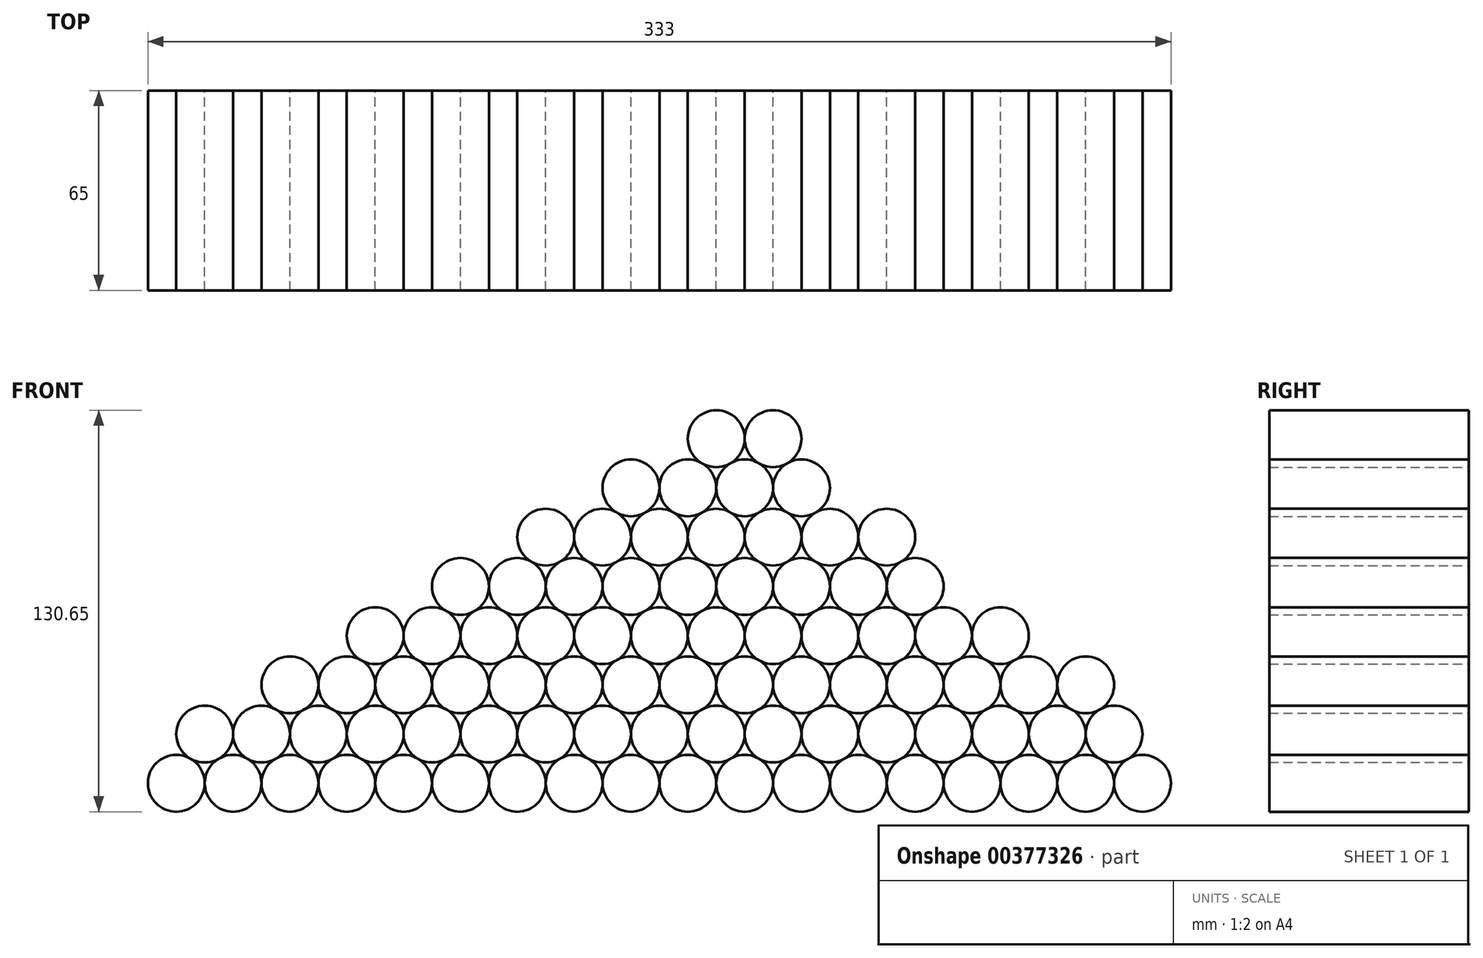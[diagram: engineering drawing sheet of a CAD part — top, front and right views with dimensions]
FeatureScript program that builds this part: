
annotation { "Feature Type Name" : "Feature", "Feature Type Description" : "" }
export const myFeature = defineFeature(function(context is Context, id is Id, definition is map)
    precondition{}
    {
        {
            var Q0;
            Q0=qCreatedBy(makeId("Front.planeOp"),FACE);
            var sketch = newSketch(context, id + "F0", { "sketchPlane" : qUnion([Q0])});
            skLineSegment(sketch, "E0", {"start": v(-257.65, 87.7) * mm, "end": v(102.35, 87.7) * mm, "construction": true});
            skLineSegment(sketch, "E1", {"start": v(16.65, 252.52) * mm, "end": v(-257.65, 87.7) * mm, "construction": true});
            skLineSegment(sketch, "E2", {"start": v(102.35, 87.7) * mm, "end": v(117.67, 100.56) * mm, "construction": true});
            skLineSegment(sketch, "E3", {"start": v(-6.85, 213.41) * mm, "end": v(16.65, 252.52) * mm, "construction": true});
            skLineSegment(sketch, "E4", {"start": v(117.67, 100.56) * mm, "end": v(-6.85, 213.41) * mm, "construction": true});
            skLineSegment(sketch, "E5", {"start": v(-226.86, 106.2) * mm, "end": v(-226.86, 87.7) * mm, "construction": true});
            skCircle(sketch, "E6", {"center": v(98.99, 96.96) * mm, "radius": 9.25 * mm});
            skCircle(sketch, "E7", {"center": v(80.49, 96.96) * mm, "radius": 9.25 * mm});
            skCircle(sketch, "E8", {"center": v(43.49, 96.96) * mm, "radius": 9.25 * mm});
            skCircle(sketch, "E9", {"center": v(24.99, 96.96) * mm, "radius": 9.25 * mm});
            skCircle(sketch, "E10", {"center": v(61.99, 96.96) * mm, "radius": 9.25 * mm});
            skCircle(sketch, "E11", {"center": v(-104.51, 96.96) * mm, "radius": 9.25 * mm});
            skCircle(sketch, "E12", {"center": v(71.24, 112.98) * mm, "radius": 9.25 * mm});
            skCircle(sketch, "E13", {"center": v(-86.01, 96.96) * mm, "radius": 9.25 * mm});
            skCircle(sketch, "E14", {"center": v(-67.51, 96.96) * mm, "radius": 9.25 * mm});
            skCircle(sketch, "E15", {"center": v(-49.01, 96.96) * mm, "radius": 9.25 * mm});
            skCircle(sketch, "E16", {"center": v(-30.51, 96.96) * mm, "radius": 9.25 * mm});
            skCircle(sketch, "E17", {"center": v(-12.01, 96.96) * mm, "radius": 9.25 * mm});
            skCircle(sketch, "E18", {"center": v(89.74, 112.98) * mm, "radius": 9.25 * mm});
            skCircle(sketch, "E19", {"center": v(6.49, 96.96) * mm, "radius": 9.25 * mm});
            skCircle(sketch, "E20", {"center": v(-215.51, 96.96) * mm, "radius": 9.25 * mm});
            skCircle(sketch, "E21", {"center": v(-197.01, 96.96) * mm, "radius": 9.25 * mm});
            skCircle(sketch, "E22", {"center": v(-169.26, 112.98) * mm, "radius": 9.25 * mm});
            skCircle(sketch, "E23", {"center": v(-178.51, 96.96) * mm, "radius": 9.25 * mm});
            skCircle(sketch, "E24", {"center": v(-160.01, 96.96) * mm, "radius": 9.25 * mm});
            skCircle(sketch, "E25", {"center": v(-141.51, 96.96) * mm, "radius": 9.25 * mm});
            skCircle(sketch, "E26", {"center": v(-123.01, 96.96) * mm, "radius": 9.25 * mm});
            skCircle(sketch, "E27", {"center": v(-187.76, 112.98) * mm, "radius": 9.25 * mm});
            skCircle(sketch, "E28", {"center": v(-150.76, 112.98) * mm, "radius": 9.25 * mm});
            skCircle(sketch, "E29", {"center": v(-132.26, 112.98) * mm, "radius": 9.25 * mm});
            skCircle(sketch, "E30", {"center": v(-113.76, 112.98) * mm, "radius": 9.25 * mm});
            skCircle(sketch, "E31", {"center": v(-76.76, 112.98) * mm, "radius": 9.25 * mm});
            skCircle(sketch, "E32", {"center": v(-95.26, 112.98) * mm, "radius": 9.25 * mm});
            skCircle(sketch, "E33", {"center": v(-141.51, 129) * mm, "radius": 9.25 * mm});
            skCircle(sketch, "E34", {"center": v(-123.01, 129) * mm, "radius": 9.25 * mm});
            skCircle(sketch, "E35", {"center": v(-104.51, 129) * mm, "radius": 9.25 * mm});
            skCircle(sketch, "E36", {"center": v(-86.01, 129) * mm, "radius": 9.25 * mm});
            skCircle(sketch, "E37", {"center": v(-160.01, 129) * mm, "radius": 9.25 * mm});
            skCircle(sketch, "E38", {"center": v(6.49, 129) * mm, "radius": 9.25 * mm});
            skCircle(sketch, "E39", {"center": v(-12.01, 129) * mm, "radius": 9.25 * mm});
            skCircle(sketch, "E40", {"center": v(-30.51, 129) * mm, "radius": 9.25 * mm});
            skCircle(sketch, "E41", {"center": v(-67.51, 129) * mm, "radius": 9.25 * mm});
            skCircle(sketch, "E42", {"center": v(-39.76, 112.98) * mm, "radius": 9.25 * mm});
            skCircle(sketch, "E43", {"center": v(-49.01, 129) * mm, "radius": 9.25 * mm});
            skCircle(sketch, "E44", {"center": v(-21.26, 112.98) * mm, "radius": 9.25 * mm});
            skCircle(sketch, "E45", {"center": v(-58.26, 112.98) * mm, "radius": 9.25 * mm});
            skCircle(sketch, "E46", {"center": v(-2.76, 112.98) * mm, "radius": 9.25 * mm});
            skCircle(sketch, "E47", {"center": v(15.74, 112.98) * mm, "radius": 9.25 * mm});
            skCircle(sketch, "E48", {"center": v(34.24, 112.98) * mm, "radius": 9.25 * mm});
            skCircle(sketch, "E49", {"center": v(52.74, 112.98) * mm, "radius": 9.25 * mm});
            skCircle(sketch, "E50", {"center": v(-95.26, 145.02) * mm, "radius": 9.25 * mm});
            skCircle(sketch, "E51", {"center": v(-76.76, 145.02) * mm, "radius": 9.25 * mm});
            skCircle(sketch, "E52", {"center": v(-58.26, 145.02) * mm, "radius": 9.25 * mm});
            skCircle(sketch, "E53", {"center": v(-39.76, 145.02) * mm, "radius": 9.25 * mm});
            skCircle(sketch, "E54", {"center": v(-21.26, 145.02) * mm, "radius": 9.25 * mm});
            skCircle(sketch, "E55", {"center": v(-2.76, 145.02) * mm, "radius": 9.25 * mm});
            skCircle(sketch, "E56", {"center": v(15.74, 145.02) * mm, "radius": 9.25 * mm});
            skCircle(sketch, "E57", {"center": v(61.99, 129) * mm, "radius": 9.25 * mm});
            skCircle(sketch, "E58", {"center": v(43.49, 129) * mm, "radius": 9.25 * mm});
            skCircle(sketch, "E59", {"center": v(24.99, 129) * mm, "radius": 9.25 * mm});
            skCircle(sketch, "E60", {"center": v(-113.76, 145.02) * mm, "radius": 9.25 * mm});
            skCircle(sketch, "E61", {"center": v(-132.26, 145.02) * mm, "radius": 9.25 * mm});
            skCircle(sketch, "E62", {"center": v(-104.51, 161.04) * mm, "radius": 9.25 * mm});
            skCircle(sketch, "E63", {"center": v(-86.01, 161.04) * mm, "radius": 9.25 * mm});
            skCircle(sketch, "E64", {"center": v(-67.51, 161.04) * mm, "radius": 9.25 * mm});
            skCircle(sketch, "E65", {"center": v(-49.01, 161.04) * mm, "radius": 9.25 * mm});
            skCircle(sketch, "E66", {"center": v(-30.51, 161.04) * mm, "radius": 9.25 * mm});
            skCircle(sketch, "E67", {"center": v(-12.01, 161.04) * mm, "radius": 9.25 * mm});
            skCircle(sketch, "E68", {"center": v(6.49, 161.04) * mm, "radius": 9.25 * mm});
            skCircle(sketch, "E69", {"center": v(34.24, 145.02) * mm, "radius": 9.25 * mm});
            skCircle(sketch, "E70", {"center": v(-76.76, 177.07) * mm, "radius": 9.25 * mm});
            skCircle(sketch, "E71", {"center": v(-2.76, 177.07) * mm, "radius": 9.25 * mm});
            skCircle(sketch, "E72", {"center": v(-21.26, 177.07) * mm, "radius": 9.25 * mm});
            skCircle(sketch, "E73", {"center": v(-39.76, 177.07) * mm, "radius": 9.25 * mm});
            skCircle(sketch, "E74", {"center": v(-30.51, 193.09) * mm, "radius": 9.25 * mm});
            skCircle(sketch, "E75", {"center": v(-58.26, 177.07) * mm, "radius": 9.25 * mm});
            skCircle(sketch, "E76", {"center": v(24.99, 161.04) * mm, "radius": 9.25 * mm});
            skCircle(sketch, "E77", {"center": v(52.74, 145.02) * mm, "radius": 9.25 * mm});
            skCircle(sketch, "E78", {"center": v(-49.01, 193.09) * mm, "radius": 9.25 * mm});
            skCircle(sketch, "E79", {"center": v(-12.01, 193.09) * mm, "radius": 9.25 * mm});
            skCircle(sketch, "E80", {"center": v(-21.26, 209.1) * mm, "radius": 9.25 * mm});
            skCircle(sketch, "E81", {"center": v(15.74, 177.07) * mm, "radius": 9.25 * mm});
            skCircle(sketch, "E82", {"center": v(-206.26, 112.98) * mm, "radius": 9.25 * mm});
            skCircle(sketch, "E83", {"center": v(-178.51, 129) * mm, "radius": 9.25 * mm});
            skCircle(sketch, "E84", {"center": v(-150.76, 145.02) * mm, "radius": 9.25 * mm});
            skCircle(sketch, "E85", {"center": v(-123.01, 161.04) * mm, "radius": 9.25 * mm});
            skCircle(sketch, "E86", {"center": v(-95.26, 177.07) * mm, "radius": 9.25 * mm});
            skCircle(sketch, "E87", {"center": v(-67.51, 193.09) * mm, "radius": 9.25 * mm});
            skCircle(sketch, "E88", {"center": v(-39.76, 209.1) * mm, "radius": 9.25 * mm});
            skCircle(sketch, "E89", {"center": v(80.49, 129) * mm, "radius": 9.25 * mm});
            skSolve(sketch);
        }
        {
            var Q0;
            {var subQ0=sQuery(id+"F0.wireOp",EDGE,"E6");var subQ1=makeQuery(id+"F0.imprint","INTERSECT",VERTEX,{"derivedFrom":[subQ0,sQuery(id+"F0.wireOp",EDGE,"E7")]});Q0=makeQuery(id+"F0.imprint","IMPRINT",FACE,{"disambiguationData":[TD([[makeQuery(id+"F0.imprint","IMPRINT",EDGE,{"disambiguationData":[TD([[subQ1,1.0]])],"derivedFrom":subQ0}),1.0]])]});}
            var Q1;
            {var subQ0=sQuery(id+"F0.wireOp",EDGE,"E77");var subQ1=makeQuery(id+"F0.imprint","INTERSECT",VERTEX,{"derivedFrom":[sQuery(id+"F0.wireOp",EDGE,"E69"),subQ0]});Q1=makeQuery(id+"F0.imprint","IMPRINT",FACE,{"disambiguationData":[TD([[makeQuery(id+"F0.imprint","IMPRINT",EDGE,{"disambiguationData":[TD([[subQ1,-1.0]])],"derivedFrom":subQ0}),1.0]])]});}
            var Q2;
            {var subQ0=sQuery(id+"F0.wireOp",EDGE,"E80");var subQ1=makeQuery(id+"F0.imprint","INTERSECT",VERTEX,{"derivedFrom":[subQ0,sQuery(id+"F0.wireOp",EDGE,"E88")]});Q2=makeQuery(id+"F0.imprint","IMPRINT",FACE,{"disambiguationData":[TD([[makeQuery(id+"F0.imprint","IMPRINT",EDGE,{"disambiguationData":[TD([[subQ1,-1.0]])],"derivedFrom":subQ0}),1.0]])]});}
            var Q3;
            {var subQ0=sQuery(id+"F0.wireOp",EDGE,"E81");var subQ1=makeQuery(id+"F0.imprint","INTERSECT",VERTEX,{"derivedFrom":[sQuery(id+"F0.wireOp",EDGE,"E71"),subQ0]});Q3=makeQuery(id+"F0.imprint","IMPRINT",FACE,{"disambiguationData":[TD([[makeQuery(id+"F0.imprint","IMPRINT",EDGE,{"disambiguationData":[TD([[subQ1,-1.0]])],"derivedFrom":subQ0}),1.0]])]});}
            var Q4;
            {var subQ0=sQuery(id+"F0.wireOp",EDGE,"E82");var subQ1=makeQuery(id+"F0.imprint","INTERSECT",VERTEX,{"derivedFrom":[sQuery(id+"F0.wireOp",EDGE,"E20"),subQ0]});Q4=makeQuery(id+"F0.imprint","IMPRINT",FACE,{"disambiguationData":[TD([[makeQuery(id+"F0.imprint","IMPRINT",EDGE,{"disambiguationData":[TD([[subQ1,1.0]])],"derivedFrom":subQ0}),1.0]])]});}
            var Q5;
            {var subQ0=sQuery(id+"F0.wireOp",EDGE,"E83");var subQ1=makeQuery(id+"F0.imprint","INTERSECT",VERTEX,{"derivedFrom":[sQuery(id+"F0.wireOp",EDGE,"E27"),subQ0]});Q5=makeQuery(id+"F0.imprint","IMPRINT",FACE,{"disambiguationData":[TD([[makeQuery(id+"F0.imprint","IMPRINT",EDGE,{"disambiguationData":[TD([[subQ1,1.0]])],"derivedFrom":subQ0}),1.0]])]});}
            var Q6;
            {var subQ0=sQuery(id+"F0.wireOp",EDGE,"E84");var subQ1=makeQuery(id+"F0.imprint","INTERSECT",VERTEX,{"derivedFrom":[sQuery(id+"F0.wireOp",EDGE,"E37"),subQ0]});Q6=makeQuery(id+"F0.imprint","IMPRINT",FACE,{"disambiguationData":[TD([[makeQuery(id+"F0.imprint","IMPRINT",EDGE,{"disambiguationData":[TD([[subQ1,1.0]])],"derivedFrom":subQ0}),1.0]])]});}
            var Q7;
            {var subQ0=sQuery(id+"F0.wireOp",EDGE,"E85");var subQ1=makeQuery(id+"F0.imprint","INTERSECT",VERTEX,{"derivedFrom":[sQuery(id+"F0.wireOp",EDGE,"E61"),subQ0]});Q7=makeQuery(id+"F0.imprint","IMPRINT",FACE,{"disambiguationData":[TD([[makeQuery(id+"F0.imprint","IMPRINT",EDGE,{"disambiguationData":[TD([[subQ1,1.0]])],"derivedFrom":subQ0}),1.0]])]});}
            var Q8;
            {var subQ0=sQuery(id+"F0.wireOp",EDGE,"E86");var subQ1=makeQuery(id+"F0.imprint","INTERSECT",VERTEX,{"derivedFrom":[sQuery(id+"F0.wireOp",EDGE,"E62"),subQ0]});Q8=makeQuery(id+"F0.imprint","IMPRINT",FACE,{"disambiguationData":[TD([[makeQuery(id+"F0.imprint","IMPRINT",EDGE,{"disambiguationData":[TD([[subQ1,1.0]])],"derivedFrom":subQ0}),1.0]])]});}
            var Q9;
            {var subQ0=sQuery(id+"F0.wireOp",EDGE,"E87");var subQ1=makeQuery(id+"F0.imprint","INTERSECT",VERTEX,{"derivedFrom":[sQuery(id+"F0.wireOp",EDGE,"E70"),subQ0]});Q9=makeQuery(id+"F0.imprint","IMPRINT",FACE,{"disambiguationData":[TD([[makeQuery(id+"F0.imprint","IMPRINT",EDGE,{"disambiguationData":[TD([[subQ1,1.0]])],"derivedFrom":subQ0}),1.0]])]});}
            var Q10;
            {var subQ0=sQuery(id+"F0.wireOp",EDGE,"E88");var subQ1=makeQuery(id+"F0.imprint","INTERSECT",VERTEX,{"derivedFrom":[sQuery(id+"F0.wireOp",EDGE,"E78"),subQ0]});Q10=makeQuery(id+"F0.imprint","IMPRINT",FACE,{"disambiguationData":[TD([[makeQuery(id+"F0.imprint","IMPRINT",EDGE,{"disambiguationData":[TD([[subQ1,1.0]])],"derivedFrom":subQ0}),1.0]])]});}
            var Q11;
            {var subQ0=sQuery(id+"F0.wireOp",EDGE,"E89");var subQ1=makeQuery(id+"F0.imprint","INTERSECT",VERTEX,{"derivedFrom":[sQuery(id+"F0.wireOp",EDGE,"E57"),subQ0]});Q11=makeQuery(id+"F0.imprint","IMPRINT",FACE,{"disambiguationData":[TD([[makeQuery(id+"F0.imprint","IMPRINT",EDGE,{"disambiguationData":[TD([[subQ1,-1.0]])],"derivedFrom":subQ0}),1.0]])]});}
            var Q12;
            {var subQ0=sQuery(id+"F0.wireOp",EDGE,"E7");var subQ1=makeQuery(id+"F0.imprint","INTERSECT",VERTEX,{"derivedFrom":[sQuery(id+"F0.wireOp",EDGE,"E6"),subQ0]});Q12=makeQuery(id+"F0.imprint","IMPRINT",FACE,{"disambiguationData":[TD([[makeQuery(id+"F0.imprint","IMPRINT",EDGE,{"disambiguationData":[TD([[subQ1,-1.0]])],"derivedFrom":subQ0}),1.0]])]});}
            var Q13;
            {var subQ0=sQuery(id+"F0.wireOp",EDGE,"E8");var subQ1=makeQuery(id+"F0.imprint","INTERSECT",VERTEX,{"derivedFrom":[subQ0,sQuery(id+"F0.wireOp",EDGE,"E10")]});Q13=makeQuery(id+"F0.imprint","IMPRINT",FACE,{"disambiguationData":[TD([[makeQuery(id+"F0.imprint","IMPRINT",EDGE,{"disambiguationData":[TD([[subQ1,-1.0]])],"derivedFrom":subQ0}),1.0]])]});}
            var Q14;
            {var subQ0=sQuery(id+"F0.wireOp",EDGE,"E9");var subQ1=makeQuery(id+"F0.imprint","INTERSECT",VERTEX,{"derivedFrom":[sQuery(id+"F0.wireOp",EDGE,"E8"),subQ0]});Q14=makeQuery(id+"F0.imprint","IMPRINT",FACE,{"disambiguationData":[TD([[makeQuery(id+"F0.imprint","IMPRINT",EDGE,{"disambiguationData":[TD([[subQ1,-1.0]])],"derivedFrom":subQ0}),1.0]])]});}
            var Q15;
            {var subQ0=sQuery(id+"F0.wireOp",EDGE,"E10");var subQ1=makeQuery(id+"F0.imprint","INTERSECT",VERTEX,{"derivedFrom":[sQuery(id+"F0.wireOp",EDGE,"E7"),subQ0]});Q15=makeQuery(id+"F0.imprint","IMPRINT",FACE,{"disambiguationData":[TD([[makeQuery(id+"F0.imprint","IMPRINT",EDGE,{"disambiguationData":[TD([[subQ1,-1.0]])],"derivedFrom":subQ0}),1.0]])]});}
            var Q16;
            {var subQ0=sQuery(id+"F0.wireOp",EDGE,"E11");var subQ1=makeQuery(id+"F0.imprint","INTERSECT",VERTEX,{"derivedFrom":[subQ0,sQuery(id+"F0.wireOp",EDGE,"E13")]});Q16=makeQuery(id+"F0.imprint","IMPRINT",FACE,{"disambiguationData":[TD([[makeQuery(id+"F0.imprint","IMPRINT",EDGE,{"disambiguationData":[TD([[subQ1,-1.0]])],"derivedFrom":subQ0}),1.0]])]});}
            var Q17;
            {var subQ0=sQuery(id+"F0.wireOp",EDGE,"E13");var subQ1=makeQuery(id+"F0.imprint","INTERSECT",VERTEX,{"derivedFrom":[subQ0,sQuery(id+"F0.wireOp",EDGE,"E14")]});Q17=makeQuery(id+"F0.imprint","IMPRINT",FACE,{"disambiguationData":[TD([[makeQuery(id+"F0.imprint","IMPRINT",EDGE,{"disambiguationData":[TD([[subQ1,-1.0]])],"derivedFrom":subQ0}),1.0]])]});}
            var Q18;
            {var subQ0=sQuery(id+"F0.wireOp",EDGE,"E14");var subQ1=makeQuery(id+"F0.imprint","INTERSECT",VERTEX,{"derivedFrom":[subQ0,sQuery(id+"F0.wireOp",EDGE,"E15")]});Q18=makeQuery(id+"F0.imprint","IMPRINT",FACE,{"disambiguationData":[TD([[makeQuery(id+"F0.imprint","IMPRINT",EDGE,{"disambiguationData":[TD([[subQ1,-1.0]])],"derivedFrom":subQ0}),1.0]])]});}
            var Q19;
            {var subQ0=sQuery(id+"F0.wireOp",EDGE,"E15");var subQ1=makeQuery(id+"F0.imprint","INTERSECT",VERTEX,{"derivedFrom":[subQ0,sQuery(id+"F0.wireOp",EDGE,"E16")]});Q19=makeQuery(id+"F0.imprint","IMPRINT",FACE,{"disambiguationData":[TD([[makeQuery(id+"F0.imprint","IMPRINT",EDGE,{"disambiguationData":[TD([[subQ1,-1.0]])],"derivedFrom":subQ0}),1.0]])]});}
            var Q20;
            {var subQ0=sQuery(id+"F0.wireOp",EDGE,"E16");var subQ1=makeQuery(id+"F0.imprint","INTERSECT",VERTEX,{"derivedFrom":[subQ0,sQuery(id+"F0.wireOp",EDGE,"E17")]});Q20=makeQuery(id+"F0.imprint","IMPRINT",FACE,{"disambiguationData":[TD([[makeQuery(id+"F0.imprint","IMPRINT",EDGE,{"disambiguationData":[TD([[subQ1,-1.0]])],"derivedFrom":subQ0}),1.0]])]});}
            var Q21;
            {var subQ0=sQuery(id+"F0.wireOp",EDGE,"E17");var subQ1=makeQuery(id+"F0.imprint","INTERSECT",VERTEX,{"derivedFrom":[subQ0,sQuery(id+"F0.wireOp",EDGE,"E19")]});Q21=makeQuery(id+"F0.imprint","IMPRINT",FACE,{"disambiguationData":[TD([[makeQuery(id+"F0.imprint","IMPRINT",EDGE,{"disambiguationData":[TD([[subQ1,-1.0]])],"derivedFrom":subQ0}),1.0]])]});}
            var Q22;
            {var subQ0=sQuery(id+"F0.wireOp",EDGE,"E18");var subQ1=makeQuery(id+"F0.imprint","INTERSECT",VERTEX,{"derivedFrom":[subQ0,sQuery(id+"F0.wireOp",EDGE,"E89")]});Q22=makeQuery(id+"F0.imprint","IMPRINT",FACE,{"disambiguationData":[TD([[makeQuery(id+"F0.imprint","IMPRINT",EDGE,{"disambiguationData":[TD([[subQ1,-1.0]])],"derivedFrom":subQ0}),1.0]])]});}
            var Q23;
            {var subQ0=sQuery(id+"F0.wireOp",EDGE,"E19");var subQ1=makeQuery(id+"F0.imprint","INTERSECT",VERTEX,{"derivedFrom":[sQuery(id+"F0.wireOp",EDGE,"E9"),subQ0]});Q23=makeQuery(id+"F0.imprint","IMPRINT",FACE,{"disambiguationData":[TD([[makeQuery(id+"F0.imprint","IMPRINT",EDGE,{"disambiguationData":[TD([[subQ1,-1.0]])],"derivedFrom":subQ0}),1.0]])]});}
            var Q24;
            {var subQ0=sQuery(id+"F0.wireOp",EDGE,"E21");var subQ1=makeQuery(id+"F0.imprint","INTERSECT",VERTEX,{"derivedFrom":[subQ0,sQuery(id+"F0.wireOp",EDGE,"E23")]});Q24=makeQuery(id+"F0.imprint","IMPRINT",FACE,{"disambiguationData":[TD([[makeQuery(id+"F0.imprint","IMPRINT",EDGE,{"disambiguationData":[TD([[subQ1,-1.0]])],"derivedFrom":subQ0}),1.0]])]});}
            var Q25;
            {var subQ0=sQuery(id+"F0.wireOp",EDGE,"E23");var subQ1=makeQuery(id+"F0.imprint","INTERSECT",VERTEX,{"derivedFrom":[subQ0,sQuery(id+"F0.wireOp",EDGE,"E24")]});Q25=makeQuery(id+"F0.imprint","IMPRINT",FACE,{"disambiguationData":[TD([[makeQuery(id+"F0.imprint","IMPRINT",EDGE,{"disambiguationData":[TD([[subQ1,-1.0]])],"derivedFrom":subQ0}),1.0]])]});}
            var Q26;
            {var subQ0=sQuery(id+"F0.wireOp",EDGE,"E24");var subQ1=makeQuery(id+"F0.imprint","INTERSECT",VERTEX,{"derivedFrom":[subQ0,sQuery(id+"F0.wireOp",EDGE,"E25")]});Q26=makeQuery(id+"F0.imprint","IMPRINT",FACE,{"disambiguationData":[TD([[makeQuery(id+"F0.imprint","IMPRINT",EDGE,{"disambiguationData":[TD([[subQ1,-1.0]])],"derivedFrom":subQ0}),1.0]])]});}
            var Q27;
            {var subQ0=sQuery(id+"F0.wireOp",EDGE,"E25");var subQ1=makeQuery(id+"F0.imprint","INTERSECT",VERTEX,{"derivedFrom":[subQ0,sQuery(id+"F0.wireOp",EDGE,"E26")]});Q27=makeQuery(id+"F0.imprint","IMPRINT",FACE,{"disambiguationData":[TD([[makeQuery(id+"F0.imprint","IMPRINT",EDGE,{"disambiguationData":[TD([[subQ1,-1.0]])],"derivedFrom":subQ0}),1.0]])]});}
            var Q28;
            {var subQ0=sQuery(id+"F0.wireOp",EDGE,"E26");var subQ1=makeQuery(id+"F0.imprint","INTERSECT",VERTEX,{"derivedFrom":[sQuery(id+"F0.wireOp",EDGE,"E11"),subQ0]});Q28=makeQuery(id+"F0.imprint","IMPRINT",FACE,{"disambiguationData":[TD([[makeQuery(id+"F0.imprint","IMPRINT",EDGE,{"disambiguationData":[TD([[subQ1,-1.0]])],"derivedFrom":subQ0}),1.0]])]});}
            var Q29;
            {var subQ0=sQuery(id+"F0.wireOp",EDGE,"E76");var subQ1=makeQuery(id+"F0.imprint","INTERSECT",VERTEX,{"derivedFrom":[subQ0,sQuery(id+"F0.wireOp",EDGE,"E81")]});Q29=makeQuery(id+"F0.imprint","IMPRINT",FACE,{"disambiguationData":[TD([[makeQuery(id+"F0.imprint","IMPRINT",EDGE,{"disambiguationData":[TD([[subQ1,-1.0]])],"derivedFrom":subQ0}),1.0]])]});}
            var Q30;
            {var subQ0=sQuery(id+"F0.wireOp",EDGE,"E79");var subQ1=makeQuery(id+"F0.imprint","INTERSECT",VERTEX,{"derivedFrom":[subQ0,sQuery(id+"F0.wireOp",EDGE,"E80")]});Q30=makeQuery(id+"F0.imprint","IMPRINT",FACE,{"disambiguationData":[TD([[makeQuery(id+"F0.imprint","IMPRINT",EDGE,{"disambiguationData":[TD([[subQ1,-1.0]])],"derivedFrom":subQ0}),1.0]])]});}
            var Q31;
            {var subQ0=sQuery(id+"F0.wireOp",EDGE,"E27");var subQ4=makeQuery(id+"F0.imprint","INTERSECT",VERTEX,{"derivedFrom":[subQ0,sQuery(id+"F0.wireOp",EDGE,"E83")]});Q31=makeQuery(id+"F0.imprint","IMPRINT",FACE,{"disambiguationData":[TD([[makeQuery(id+"F0.imprint","IMPRINT",EDGE,{"disambiguationData":[TD([[subQ4,1.0]])],"derivedFrom":subQ0}),1.0]])]});}
            var Q32;
            {var subQ0=sQuery(id+"F0.wireOp",EDGE,"E37");var subQ4=makeQuery(id+"F0.imprint","INTERSECT",VERTEX,{"derivedFrom":[subQ0,sQuery(id+"F0.wireOp",EDGE,"E84")]});Q32=makeQuery(id+"F0.imprint","IMPRINT",FACE,{"disambiguationData":[TD([[makeQuery(id+"F0.imprint","IMPRINT",EDGE,{"disambiguationData":[TD([[subQ4,1.0]])],"derivedFrom":subQ0}),1.0]])]});}
            var Q33;
            {var subQ0=sQuery(id+"F0.wireOp",EDGE,"E57");var subQ4=makeQuery(id+"F0.imprint","INTERSECT",VERTEX,{"derivedFrom":[subQ0,sQuery(id+"F0.wireOp",EDGE,"E77")]});Q33=makeQuery(id+"F0.imprint","IMPRINT",FACE,{"disambiguationData":[TD([[makeQuery(id+"F0.imprint","IMPRINT",EDGE,{"disambiguationData":[TD([[subQ4,1.0]])],"derivedFrom":subQ0}),1.0]])]});}
            var Q34;
            {var subQ0=sQuery(id+"F0.wireOp",EDGE,"E61");var subQ4=makeQuery(id+"F0.imprint","INTERSECT",VERTEX,{"derivedFrom":[subQ0,sQuery(id+"F0.wireOp",EDGE,"E85")]});Q34=makeQuery(id+"F0.imprint","IMPRINT",FACE,{"disambiguationData":[TD([[makeQuery(id+"F0.imprint","IMPRINT",EDGE,{"disambiguationData":[TD([[subQ4,1.0]])],"derivedFrom":subQ0}),1.0]])]});}
            var Q35;
            {var subQ0=sQuery(id+"F0.wireOp",EDGE,"E62");var subQ4=makeQuery(id+"F0.imprint","INTERSECT",VERTEX,{"derivedFrom":[subQ0,sQuery(id+"F0.wireOp",EDGE,"E86")]});Q35=makeQuery(id+"F0.imprint","IMPRINT",FACE,{"disambiguationData":[TD([[makeQuery(id+"F0.imprint","IMPRINT",EDGE,{"disambiguationData":[TD([[subQ4,1.0]])],"derivedFrom":subQ0}),1.0]])]});}
            var Q36;
            {var subQ0=sQuery(id+"F0.wireOp",EDGE,"E69");var subQ4=makeQuery(id+"F0.imprint","INTERSECT",VERTEX,{"derivedFrom":[subQ0,sQuery(id+"F0.wireOp",EDGE,"E76")]});Q36=makeQuery(id+"F0.imprint","IMPRINT",FACE,{"disambiguationData":[TD([[makeQuery(id+"F0.imprint","IMPRINT",EDGE,{"disambiguationData":[TD([[subQ4,1.0]])],"derivedFrom":subQ0}),1.0]])]});}
            var Q37;
            {var subQ0=sQuery(id+"F0.wireOp",EDGE,"E70");var subQ4=makeQuery(id+"F0.imprint","INTERSECT",VERTEX,{"derivedFrom":[subQ0,sQuery(id+"F0.wireOp",EDGE,"E87")]});Q37=makeQuery(id+"F0.imprint","IMPRINT",FACE,{"disambiguationData":[TD([[makeQuery(id+"F0.imprint","IMPRINT",EDGE,{"disambiguationData":[TD([[subQ4,1.0]])],"derivedFrom":subQ0}),1.0]])]});}
            var Q38;
            {var subQ0=sQuery(id+"F0.wireOp",EDGE,"E71");var subQ4=makeQuery(id+"F0.imprint","INTERSECT",VERTEX,{"derivedFrom":[subQ0,sQuery(id+"F0.wireOp",EDGE,"E79")]});Q38=makeQuery(id+"F0.imprint","IMPRINT",FACE,{"disambiguationData":[TD([[makeQuery(id+"F0.imprint","IMPRINT",EDGE,{"disambiguationData":[TD([[subQ4,1.0]])],"derivedFrom":subQ0}),1.0]])]});}
            var Q39;
            {var subQ0=sQuery(id+"F0.wireOp",EDGE,"E78");var subQ4=makeQuery(id+"F0.imprint","INTERSECT",VERTEX,{"derivedFrom":[subQ0,sQuery(id+"F0.wireOp",EDGE,"E88")]});Q39=makeQuery(id+"F0.imprint","IMPRINT",FACE,{"disambiguationData":[TD([[makeQuery(id+"F0.imprint","IMPRINT",EDGE,{"disambiguationData":[TD([[subQ4,1.0]])],"derivedFrom":subQ0}),1.0]])]});}
            var Q40;
            {var subQ0=sQuery(id+"F0.wireOp",EDGE,"E51");var subQ4=makeQuery(id+"F0.imprint","INTERSECT",VERTEX,{"derivedFrom":[subQ0,sQuery(id+"F0.wireOp",EDGE,"E64")]});Q40=makeQuery(id+"F0.imprint","IMPRINT",FACE,{"disambiguationData":[TD([[makeQuery(id+"F0.imprint","IMPRINT",EDGE,{"disambiguationData":[TD([[subQ4,1.0]])],"derivedFrom":subQ0}),1.0]])]});}
            var Q41;
            {var subQ0=sQuery(id+"F0.wireOp",EDGE,"E59");var subQ5=makeQuery(id+"F0.imprint","INTERSECT",VERTEX,{"derivedFrom":[sQuery(id+"F0.wireOp",EDGE,"E58"),subQ0]});Q41=makeQuery(id+"F0.imprint","IMPRINT",FACE,{"disambiguationData":[TD([[makeQuery(id+"F0.imprint","IMPRINT",EDGE,{"disambiguationData":[TD([[subQ5,-1.0]])],"derivedFrom":subQ0}),1.0]])]});}
            var Q42;
            {var subQ0=sQuery(id+"F0.wireOp",EDGE,"E48");var subQ4=makeQuery(id+"F0.imprint","INTERSECT",VERTEX,{"derivedFrom":[subQ0,sQuery(id+"F0.wireOp",EDGE,"E58")]});Q42=makeQuery(id+"F0.imprint","IMPRINT",FACE,{"disambiguationData":[TD([[makeQuery(id+"F0.imprint","IMPRINT",EDGE,{"disambiguationData":[TD([[subQ4,1.0]])],"derivedFrom":subQ0}),1.0]])]});}
            var Q43;
            {var subQ0=sQuery(id+"F0.wireOp",EDGE,"E46");var subQ4=makeQuery(id+"F0.imprint","INTERSECT",VERTEX,{"derivedFrom":[sQuery(id+"F0.wireOp",EDGE,"E38"),subQ0]});Q43=makeQuery(id+"F0.imprint","IMPRINT",FACE,{"disambiguationData":[TD([[makeQuery(id+"F0.imprint","IMPRINT",EDGE,{"disambiguationData":[TD([[subQ4,1.0]])],"derivedFrom":subQ0}),1.0]])]});}
            var Q44;
            {var subQ0=sQuery(id+"F0.wireOp",EDGE,"E39");var subQ5=makeQuery(id+"F0.imprint","INTERSECT",VERTEX,{"derivedFrom":[sQuery(id+"F0.wireOp",EDGE,"E38"),subQ0]});Q44=makeQuery(id+"F0.imprint","IMPRINT",FACE,{"disambiguationData":[TD([[makeQuery(id+"F0.imprint","IMPRINT",EDGE,{"disambiguationData":[TD([[subQ5,-1.0]])],"derivedFrom":subQ0}),1.0]])]});}
            var Q45;
            {var subQ0=sQuery(id+"F0.wireOp",EDGE,"E49");var subQ5=makeQuery(id+"F0.imprint","INTERSECT",VERTEX,{"derivedFrom":[sQuery(id+"F0.wireOp",EDGE,"E12"),subQ0]});Q45=makeQuery(id+"F0.imprint","IMPRINT",FACE,{"disambiguationData":[TD([[makeQuery(id+"F0.imprint","IMPRINT",EDGE,{"disambiguationData":[TD([[subQ5,-1.0]])],"derivedFrom":subQ0}),1.0]])]});}
            var Q46;
            {var subQ0=sQuery(id+"F0.wireOp",EDGE,"E55");var subQ4=makeQuery(id+"F0.imprint","INTERSECT",VERTEX,{"derivedFrom":[subQ0,sQuery(id+"F0.wireOp",EDGE,"E68")]});Q46=makeQuery(id+"F0.imprint","IMPRINT",FACE,{"disambiguationData":[TD([[makeQuery(id+"F0.imprint","IMPRINT",EDGE,{"disambiguationData":[TD([[subQ4,1.0]])],"derivedFrom":subQ0}),1.0]])]});}
            var Q47;
            {var subQ0=sQuery(id+"F0.wireOp",EDGE,"E73");var subQ5=makeQuery(id+"F0.imprint","INTERSECT",VERTEX,{"derivedFrom":[sQuery(id+"F0.wireOp",EDGE,"E72"),subQ0]});Q47=makeQuery(id+"F0.imprint","IMPRINT",FACE,{"disambiguationData":[TD([[makeQuery(id+"F0.imprint","IMPRINT",EDGE,{"disambiguationData":[TD([[subQ5,-1.0]])],"derivedFrom":subQ0}),1.0]])]});}
            var Q48;
            {var subQ0=sQuery(id+"F0.wireOp",EDGE,"E34");var subQ4=makeQuery(id+"F0.imprint","INTERSECT",VERTEX,{"derivedFrom":[subQ0,sQuery(id+"F0.wireOp",EDGE,"E60")]});Q48=makeQuery(id+"F0.imprint","IMPRINT",FACE,{"disambiguationData":[TD([[makeQuery(id+"F0.imprint","IMPRINT",EDGE,{"disambiguationData":[TD([[subQ4,1.0]])],"derivedFrom":subQ0}),1.0]])]});}
            var Q49;
            {var subQ0=sQuery(id+"F0.wireOp",EDGE,"E67");var subQ4=makeQuery(id+"F0.imprint","INTERSECT",VERTEX,{"derivedFrom":[subQ0,sQuery(id+"F0.wireOp",EDGE,"E71")]});Q49=makeQuery(id+"F0.imprint","IMPRINT",FACE,{"disambiguationData":[TD([[makeQuery(id+"F0.imprint","IMPRINT",EDGE,{"disambiguationData":[TD([[subQ4,1.0]])],"derivedFrom":subQ0}),1.0]])]});}
            var Q50;
            {var subQ0=sQuery(id+"F0.wireOp",EDGE,"E31");var subQ4=makeQuery(id+"F0.imprint","INTERSECT",VERTEX,{"derivedFrom":[subQ0,sQuery(id+"F0.wireOp",EDGE,"E41")]});Q50=makeQuery(id+"F0.imprint","IMPRINT",FACE,{"disambiguationData":[TD([[makeQuery(id+"F0.imprint","IMPRINT",EDGE,{"disambiguationData":[TD([[subQ4,1.0]])],"derivedFrom":subQ0}),1.0]])]});}
            var Q51;
            {var subQ0=sQuery(id+"F0.wireOp",EDGE,"E41");var subQ4=makeQuery(id+"F0.imprint","INTERSECT",VERTEX,{"derivedFrom":[subQ0,sQuery(id+"F0.wireOp",EDGE,"E52")]});Q51=makeQuery(id+"F0.imprint","IMPRINT",FACE,{"disambiguationData":[TD([[makeQuery(id+"F0.imprint","IMPRINT",EDGE,{"disambiguationData":[TD([[subQ4,1.0]])],"derivedFrom":subQ0}),1.0]])]});}
            var Q52;
            {var subQ0=sQuery(id+"F0.wireOp",EDGE,"E74");var subQ4=makeQuery(id+"F0.imprint","INTERSECT",VERTEX,{"derivedFrom":[subQ0,sQuery(id+"F0.wireOp",EDGE,"E80")]});Q52=makeQuery(id+"F0.imprint","IMPRINT",FACE,{"disambiguationData":[TD([[makeQuery(id+"F0.imprint","IMPRINT",EDGE,{"disambiguationData":[TD([[subQ4,1.0]])],"derivedFrom":subQ0}),1.0]])]});}
            var Q53;
            {var subQ0=sQuery(id+"F0.wireOp",EDGE,"E63");var subQ4=makeQuery(id+"F0.imprint","INTERSECT",VERTEX,{"derivedFrom":[subQ0,sQuery(id+"F0.wireOp",EDGE,"E70")]});Q53=makeQuery(id+"F0.imprint","IMPRINT",FACE,{"disambiguationData":[TD([[makeQuery(id+"F0.imprint","IMPRINT",EDGE,{"disambiguationData":[TD([[subQ4,1.0]])],"derivedFrom":subQ0}),1.0]])]});}
            var Q54;
            {var subQ0=sQuery(id+"F0.wireOp",EDGE,"E58");var subQ5=makeQuery(id+"F0.imprint","INTERSECT",VERTEX,{"derivedFrom":[sQuery(id+"F0.wireOp",EDGE,"E57"),subQ0]});Q54=makeQuery(id+"F0.imprint","IMPRINT",FACE,{"disambiguationData":[TD([[makeQuery(id+"F0.imprint","IMPRINT",EDGE,{"disambiguationData":[TD([[subQ5,-1.0]])],"derivedFrom":subQ0}),1.0]])]});}
            var Q55;
            {var subQ0=sQuery(id+"F0.wireOp",EDGE,"E56");var subQ4=makeQuery(id+"F0.imprint","INTERSECT",VERTEX,{"derivedFrom":[subQ0,sQuery(id+"F0.wireOp",EDGE,"E76")]});Q55=makeQuery(id+"F0.imprint","IMPRINT",FACE,{"disambiguationData":[TD([[makeQuery(id+"F0.imprint","IMPRINT",EDGE,{"disambiguationData":[TD([[subQ4,1.0]])],"derivedFrom":subQ0}),1.0]])]});}
            var Q56;
            {var subQ0=sQuery(id+"F0.wireOp",EDGE,"E50");var subQ4=makeQuery(id+"F0.imprint","INTERSECT",VERTEX,{"derivedFrom":[subQ0,sQuery(id+"F0.wireOp",EDGE,"E63")]});Q56=makeQuery(id+"F0.imprint","IMPRINT",FACE,{"disambiguationData":[TD([[makeQuery(id+"F0.imprint","IMPRINT",EDGE,{"disambiguationData":[TD([[subQ4,1.0]])],"derivedFrom":subQ0}),1.0]])]});}
            var Q57;
            {var subQ0=sQuery(id+"F0.wireOp",EDGE,"E42");var subQ4=makeQuery(id+"F0.imprint","INTERSECT",VERTEX,{"derivedFrom":[sQuery(id+"F0.wireOp",EDGE,"E40"),subQ0]});Q57=makeQuery(id+"F0.imprint","IMPRINT",FACE,{"disambiguationData":[TD([[makeQuery(id+"F0.imprint","IMPRINT",EDGE,{"disambiguationData":[TD([[subQ4,1.0]])],"derivedFrom":subQ0}),1.0]])]});}
            var Q58;
            {var subQ0=sQuery(id+"F0.wireOp",EDGE,"E47");var subQ4=makeQuery(id+"F0.imprint","INTERSECT",VERTEX,{"derivedFrom":[subQ0,sQuery(id+"F0.wireOp",EDGE,"E59")]});Q58=makeQuery(id+"F0.imprint","IMPRINT",FACE,{"disambiguationData":[TD([[makeQuery(id+"F0.imprint","IMPRINT",EDGE,{"disambiguationData":[TD([[subQ4,1.0]])],"derivedFrom":subQ0}),1.0]])]});}
            var Q59;
            {var subQ0=sQuery(id+"F0.wireOp",EDGE,"E52");var subQ4=makeQuery(id+"F0.imprint","INTERSECT",VERTEX,{"derivedFrom":[subQ0,sQuery(id+"F0.wireOp",EDGE,"E65")]});Q59=makeQuery(id+"F0.imprint","IMPRINT",FACE,{"disambiguationData":[TD([[makeQuery(id+"F0.imprint","IMPRINT",EDGE,{"disambiguationData":[TD([[subQ4,1.0]])],"derivedFrom":subQ0}),1.0]])]});}
            var Q60;
            {var subQ0=sQuery(id+"F0.wireOp",EDGE,"E33");var subQ4=makeQuery(id+"F0.imprint","INTERSECT",VERTEX,{"derivedFrom":[subQ0,sQuery(id+"F0.wireOp",EDGE,"E61")]});Q60=makeQuery(id+"F0.imprint","IMPRINT",FACE,{"disambiguationData":[TD([[makeQuery(id+"F0.imprint","IMPRINT",EDGE,{"disambiguationData":[TD([[subQ4,1.0]])],"derivedFrom":subQ0}),1.0]])]});}
            var Q61;
            {var subQ0=sQuery(id+"F0.wireOp",EDGE,"E30");var subQ4=makeQuery(id+"F0.imprint","INTERSECT",VERTEX,{"derivedFrom":[subQ0,sQuery(id+"F0.wireOp",EDGE,"E35")]});Q61=makeQuery(id+"F0.imprint","IMPRINT",FACE,{"disambiguationData":[TD([[makeQuery(id+"F0.imprint","IMPRINT",EDGE,{"disambiguationData":[TD([[subQ4,1.0]])],"derivedFrom":subQ0}),1.0]])]});}
            var Q62;
            {var subQ0=sQuery(id+"F0.wireOp",EDGE,"E32");var subQ5=makeQuery(id+"F0.imprint","INTERSECT",VERTEX,{"derivedFrom":[sQuery(id+"F0.wireOp",EDGE,"E31"),subQ0]});Q62=makeQuery(id+"F0.imprint","IMPRINT",FACE,{"disambiguationData":[TD([[makeQuery(id+"F0.imprint","IMPRINT",EDGE,{"disambiguationData":[TD([[subQ5,-1.0]])],"derivedFrom":subQ0}),1.0]])]});}
            var Q63;
            {var subQ0=sQuery(id+"F0.wireOp",EDGE,"E29");var subQ4=makeQuery(id+"F0.imprint","INTERSECT",VERTEX,{"derivedFrom":[subQ0,sQuery(id+"F0.wireOp",EDGE,"E34")]});Q63=makeQuery(id+"F0.imprint","IMPRINT",FACE,{"disambiguationData":[TD([[makeQuery(id+"F0.imprint","IMPRINT",EDGE,{"disambiguationData":[TD([[subQ4,1.0]])],"derivedFrom":subQ0}),1.0]])]});}
            var Q64;
            {var subQ0=sQuery(id+"F0.wireOp",EDGE,"E68");var subQ4=makeQuery(id+"F0.imprint","INTERSECT",VERTEX,{"derivedFrom":[subQ0,sQuery(id+"F0.wireOp",EDGE,"E81")]});Q64=makeQuery(id+"F0.imprint","IMPRINT",FACE,{"disambiguationData":[TD([[makeQuery(id+"F0.imprint","IMPRINT",EDGE,{"disambiguationData":[TD([[subQ4,1.0]])],"derivedFrom":subQ0}),1.0]])]});}
            var Q65;
            {var subQ0=sQuery(id+"F0.wireOp",EDGE,"E35");var subQ4=makeQuery(id+"F0.imprint","INTERSECT",VERTEX,{"derivedFrom":[subQ0,sQuery(id+"F0.wireOp",EDGE,"E50")]});Q65=makeQuery(id+"F0.imprint","IMPRINT",FACE,{"disambiguationData":[TD([[makeQuery(id+"F0.imprint","IMPRINT",EDGE,{"disambiguationData":[TD([[subQ4,1.0]])],"derivedFrom":subQ0}),1.0]])]});}
            var Q66;
            {var subQ0=sQuery(id+"F0.wireOp",EDGE,"E40");var subQ5=makeQuery(id+"F0.imprint","INTERSECT",VERTEX,{"derivedFrom":[sQuery(id+"F0.wireOp",EDGE,"E39"),subQ0]});Q66=makeQuery(id+"F0.imprint","IMPRINT",FACE,{"disambiguationData":[TD([[makeQuery(id+"F0.imprint","IMPRINT",EDGE,{"disambiguationData":[TD([[subQ5,-1.0]])],"derivedFrom":subQ0}),1.0]])]});}
            var Q67;
            {var subQ0=sQuery(id+"F0.wireOp",EDGE,"E65");var subQ4=makeQuery(id+"F0.imprint","INTERSECT",VERTEX,{"derivedFrom":[subQ0,sQuery(id+"F0.wireOp",EDGE,"E73")]});Q67=makeQuery(id+"F0.imprint","IMPRINT",FACE,{"disambiguationData":[TD([[makeQuery(id+"F0.imprint","IMPRINT",EDGE,{"disambiguationData":[TD([[subQ4,1.0]])],"derivedFrom":subQ0}),1.0]])]});}
            var Q68;
            {var subQ0=sQuery(id+"F0.wireOp",EDGE,"E66");var subQ4=makeQuery(id+"F0.imprint","INTERSECT",VERTEX,{"derivedFrom":[subQ0,sQuery(id+"F0.wireOp",EDGE,"E72")]});Q68=makeQuery(id+"F0.imprint","IMPRINT",FACE,{"disambiguationData":[TD([[makeQuery(id+"F0.imprint","IMPRINT",EDGE,{"disambiguationData":[TD([[subQ4,1.0]])],"derivedFrom":subQ0}),1.0]])]});}
            var Q69;
            {var subQ0=sQuery(id+"F0.wireOp",EDGE,"E72");var subQ5=makeQuery(id+"F0.imprint","INTERSECT",VERTEX,{"derivedFrom":[sQuery(id+"F0.wireOp",EDGE,"E71"),subQ0]});Q69=makeQuery(id+"F0.imprint","IMPRINT",FACE,{"disambiguationData":[TD([[makeQuery(id+"F0.imprint","IMPRINT",EDGE,{"disambiguationData":[TD([[subQ5,-1.0]])],"derivedFrom":subQ0}),1.0]])]});}
            var Q70;
            {var subQ0=sQuery(id+"F0.wireOp",EDGE,"E28");var subQ4=makeQuery(id+"F0.imprint","INTERSECT",VERTEX,{"derivedFrom":[subQ0,sQuery(id+"F0.wireOp",EDGE,"E33")]});Q70=makeQuery(id+"F0.imprint","IMPRINT",FACE,{"disambiguationData":[TD([[makeQuery(id+"F0.imprint","IMPRINT",EDGE,{"disambiguationData":[TD([[subQ4,1.0]])],"derivedFrom":subQ0}),1.0]])]});}
            var Q71;
            {var subQ0=sQuery(id+"F0.wireOp",EDGE,"E53");var subQ4=makeQuery(id+"F0.imprint","INTERSECT",VERTEX,{"derivedFrom":[subQ0,sQuery(id+"F0.wireOp",EDGE,"E66")]});Q71=makeQuery(id+"F0.imprint","IMPRINT",FACE,{"disambiguationData":[TD([[makeQuery(id+"F0.imprint","IMPRINT",EDGE,{"disambiguationData":[TD([[subQ4,1.0]])],"derivedFrom":subQ0}),1.0]])]});}
            var Q72;
            {var subQ0=sQuery(id+"F0.wireOp",EDGE,"E12");var subQ4=makeQuery(id+"F0.imprint","INTERSECT",VERTEX,{"derivedFrom":[subQ0,sQuery(id+"F0.wireOp",EDGE,"E89")]});Q72=makeQuery(id+"F0.imprint","IMPRINT",FACE,{"disambiguationData":[TD([[makeQuery(id+"F0.imprint","IMPRINT",EDGE,{"disambiguationData":[TD([[subQ4,1.0]])],"derivedFrom":subQ0}),1.0]])]});}
            var Q73;
            {var subQ0=sQuery(id+"F0.wireOp",EDGE,"E44");var subQ4=makeQuery(id+"F0.imprint","INTERSECT",VERTEX,{"derivedFrom":[sQuery(id+"F0.wireOp",EDGE,"E39"),subQ0]});Q73=makeQuery(id+"F0.imprint","IMPRINT",FACE,{"disambiguationData":[TD([[makeQuery(id+"F0.imprint","IMPRINT",EDGE,{"disambiguationData":[TD([[subQ4,1.0]])],"derivedFrom":subQ0}),1.0]])]});}
            var Q74;
            {var subQ0=sQuery(id+"F0.wireOp",EDGE,"E45");var subQ5=makeQuery(id+"F0.imprint","INTERSECT",VERTEX,{"derivedFrom":[sQuery(id+"F0.wireOp",EDGE,"E42"),subQ0]});Q74=makeQuery(id+"F0.imprint","IMPRINT",FACE,{"disambiguationData":[TD([[makeQuery(id+"F0.imprint","IMPRINT",EDGE,{"disambiguationData":[TD([[subQ5,-1.0]])],"derivedFrom":subQ0}),1.0]])]});}
            var Q75;
            {var subQ0=sQuery(id+"F0.wireOp",EDGE,"E75");var subQ5=makeQuery(id+"F0.imprint","INTERSECT",VERTEX,{"derivedFrom":[sQuery(id+"F0.wireOp",EDGE,"E73"),subQ0]});Q75=makeQuery(id+"F0.imprint","IMPRINT",FACE,{"disambiguationData":[TD([[makeQuery(id+"F0.imprint","IMPRINT",EDGE,{"disambiguationData":[TD([[subQ5,-1.0]])],"derivedFrom":subQ0}),1.0]])]});}
            var Q76;
            {var subQ0=sQuery(id+"F0.wireOp",EDGE,"E64");var subQ4=makeQuery(id+"F0.imprint","INTERSECT",VERTEX,{"derivedFrom":[subQ0,sQuery(id+"F0.wireOp",EDGE,"E75")]});Q76=makeQuery(id+"F0.imprint","IMPRINT",FACE,{"disambiguationData":[TD([[makeQuery(id+"F0.imprint","IMPRINT",EDGE,{"disambiguationData":[TD([[subQ4,1.0]])],"derivedFrom":subQ0}),1.0]])]});}
            var Q77;
            {var subQ0=sQuery(id+"F0.wireOp",EDGE,"E22");var subQ4=makeQuery(id+"F0.imprint","INTERSECT",VERTEX,{"derivedFrom":[subQ0,sQuery(id+"F0.wireOp",EDGE,"E37")]});Q77=makeQuery(id+"F0.imprint","IMPRINT",FACE,{"disambiguationData":[TD([[makeQuery(id+"F0.imprint","IMPRINT",EDGE,{"disambiguationData":[TD([[subQ4,1.0]])],"derivedFrom":subQ0}),1.0]])]});}
            var Q78;
            {var subQ0=sQuery(id+"F0.wireOp",EDGE,"E60");var subQ5=makeQuery(id+"F0.imprint","INTERSECT",VERTEX,{"derivedFrom":[sQuery(id+"F0.wireOp",EDGE,"E50"),subQ0]});Q78=makeQuery(id+"F0.imprint","IMPRINT",FACE,{"disambiguationData":[TD([[makeQuery(id+"F0.imprint","IMPRINT",EDGE,{"disambiguationData":[TD([[subQ5,-1.0]])],"derivedFrom":subQ0}),1.0]])]});}
            var Q79;
            {var subQ0=sQuery(id+"F0.wireOp",EDGE,"E36");var subQ4=makeQuery(id+"F0.imprint","INTERSECT",VERTEX,{"derivedFrom":[subQ0,sQuery(id+"F0.wireOp",EDGE,"E51")]});Q79=makeQuery(id+"F0.imprint","IMPRINT",FACE,{"disambiguationData":[TD([[makeQuery(id+"F0.imprint","IMPRINT",EDGE,{"disambiguationData":[TD([[subQ4,1.0]])],"derivedFrom":subQ0}),1.0]])]});}
            var Q80;
            {var subQ0=sQuery(id+"F0.wireOp",EDGE,"E54");var subQ4=makeQuery(id+"F0.imprint","INTERSECT",VERTEX,{"derivedFrom":[subQ0,sQuery(id+"F0.wireOp",EDGE,"E67")]});Q80=makeQuery(id+"F0.imprint","IMPRINT",FACE,{"disambiguationData":[TD([[makeQuery(id+"F0.imprint","IMPRINT",EDGE,{"disambiguationData":[TD([[subQ4,1.0]])],"derivedFrom":subQ0}),1.0]])]});}
            var Q81;
            {var subQ0=sQuery(id+"F0.wireOp",EDGE,"E43");var subQ5=makeQuery(id+"F0.imprint","INTERSECT",VERTEX,{"derivedFrom":[sQuery(id+"F0.wireOp",EDGE,"E40"),subQ0]});Q81=makeQuery(id+"F0.imprint","IMPRINT",FACE,{"disambiguationData":[TD([[makeQuery(id+"F0.imprint","IMPRINT",EDGE,{"disambiguationData":[TD([[subQ5,-1.0]])],"derivedFrom":subQ0}),1.0]])]});}
            var Q82;
            {var subQ0=sQuery(id+"F0.wireOp",EDGE,"E38");var subQ4=makeQuery(id+"F0.imprint","INTERSECT",VERTEX,{"derivedFrom":[subQ0,sQuery(id+"F0.wireOp",EDGE,"E56")]});Q82=makeQuery(id+"F0.imprint","IMPRINT",FACE,{"disambiguationData":[TD([[makeQuery(id+"F0.imprint","IMPRINT",EDGE,{"disambiguationData":[TD([[subQ4,1.0]])],"derivedFrom":subQ0}),1.0]])]});}
            var Q83;
            {var subQ0=sQuery(id+"F0.wireOp",EDGE,"E20");var subQ1=makeQuery(id+"F0.imprint","INTERSECT",VERTEX,{"derivedFrom":[subQ0,sQuery(id+"F0.wireOp",EDGE,"E21")]});Q83=makeQuery(id+"F0.imprint","IMPRINT",FACE,{"disambiguationData":[TD([[makeQuery(id+"F0.imprint","IMPRINT",EDGE,{"disambiguationData":[TD([[subQ1,-1.0]])],"derivedFrom":subQ0}),1.0]])]});}
            extrude(context, id + "F1", {"entities" : qUnion([Q0, Q1, Q2, Q3, Q4, Q5, Q6, Q7, Q8, Q9, Q10, Q11, Q12, Q13, Q14, Q15, Q16, Q17, Q18, Q19, Q20, Q21, Q22, Q23, Q24, Q25, Q26, Q27, Q28, Q29, Q30, Q31, Q32, Q33, Q34, Q35, Q36, Q37, Q38, Q39, Q40, Q41, Q42, Q43, Q44, Q45, Q46, Q47, Q48, Q49, Q50, Q51, Q52, Q53, Q54, Q55, Q56, Q57, Q58, Q59, Q60, Q61, Q62, Q63, Q64, Q65, Q66, Q67, Q68, Q69, Q70, Q71, Q72, Q73, Q74, Q75, Q76, Q77, Q78, Q79, Q80, Q81, Q82, Q83]), "depth" : 65 * mm});
        }
    });
